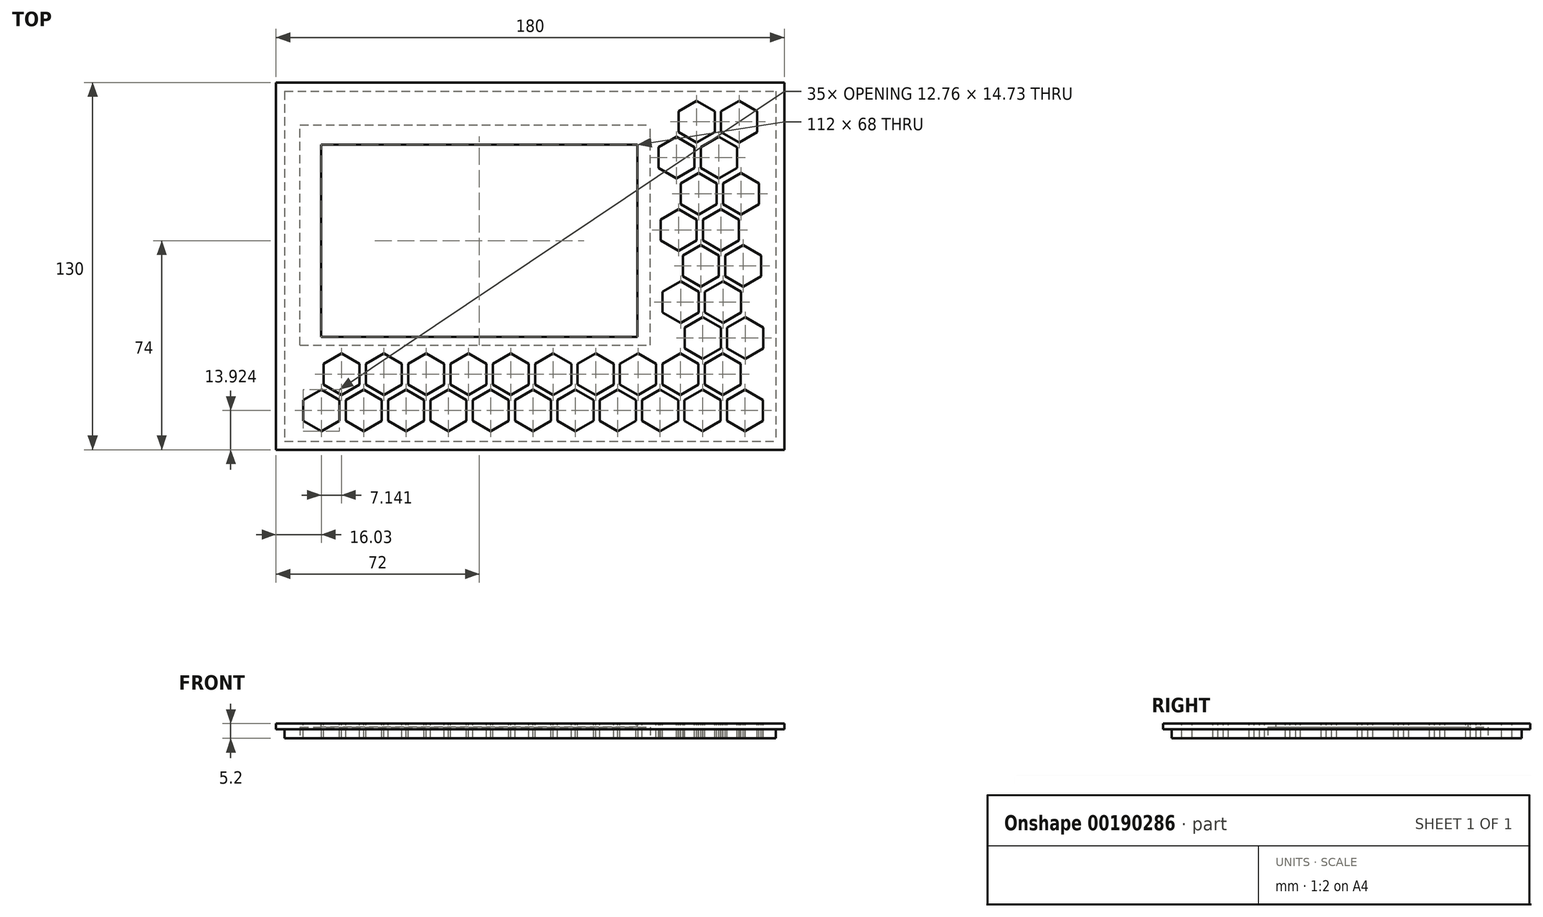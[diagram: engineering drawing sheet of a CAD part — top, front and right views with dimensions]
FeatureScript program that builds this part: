
annotation { "Feature Type Name" : "Feature", "Feature Type Description" : "" }
export const myFeature = defineFeature(function(context is Context, id is Id, definition is map)
    precondition{}
    {
        {
            var Q0;
            Q0=qCreatedBy(makeId("Top.planeOp"),FACE);
            var sketch = newSketch(context, id + "F0", { "sketchPlane" : qUnion([Q0])});
            skLineSegment(sketch, "E0.bottom", {"start": v(42.5, 28) * mm, "end": v(-42.5, 28) * mm});
            skLineSegment(sketch, "E0.top", {"start": v(42.5, -28) * mm, "end": v(-42.5, -28) * mm});
            skLineSegment(sketch, "E0.left", {"start": v(42.5, 28) * mm, "end": v(42.5, -28) * mm});
            skLineSegment(sketch, "E0.right", {"start": v(-42.5, 28) * mm, "end": v(-42.5, -28) * mm});
            skPoint(sketch, "E0.middle", {"position": v(0, 0) * mm});
            skCircle(sketch, "E1", {"center": v(-39, 24.5) * mm, "radius": 1.4 * mm});
            skCircle(sketch, "E2.MirrorC", {"center": v(-34.56, -24.5) * mm, "radius": 1.4 * mm});
            skCircle(sketch, "E3", {"center": v(19, 24.5) * mm, "radius": 1.4 * mm});
            skCircle(sketch, "E4.MirrorC", {"center": v(19, -24.7) * mm, "radius": 1.4 * mm});
            skSolve(sketch);
        }
        {
            var Q0;
            Q0=qCreatedBy(makeId("Top.planeOp"),FACE);
            var sketch = newSketch(context, id + "F1", { "sketchPlane" : qUnion([Q0])});
            skLineSegment(sketch, "E5.bottom", {"start": v(-90, 65) * mm, "end": v(90, 65) * mm});
            skLineSegment(sketch, "E5.top", {"start": v(-90, -65) * mm, "end": v(90, -65) * mm});
            skLineSegment(sketch, "E5.left", {"start": v(-90, 65) * mm, "end": v(-90, -65) * mm});
            skLineSegment(sketch, "E5.right", {"start": v(90, 65) * mm, "end": v(90, -65) * mm});
            skPoint(sketch, "E5.middle", {"position": v(0, 0) * mm});
            skLineSegment(sketch, "E6.bottom", {"start": v(-86.95, 61.95) * mm, "end": v(86.95, 61.95) * mm});
            skLineSegment(sketch, "E6.top", {"start": v(-86.95, -61.95) * mm, "end": v(86.95, -61.95) * mm});
            skLineSegment(sketch, "E6.left", {"start": v(-86.95, 61.95) * mm, "end": v(-86.95, -61.95) * mm});
            skLineSegment(sketch, "E6.right", {"start": v(86.95, 61.95) * mm, "end": v(86.95, -61.95) * mm});
            skSolve(sketch);
        }
        {
            var Q0;
            Q0=qCreatedBy(makeId("Top.planeOp"),FACE);
            var sketch = newSketch(context, id + "F2", { "sketchPlane" : qUnion([Q0])});
            skLineSegment(sketch, "E7.bottom", {"start": v(42.5, 50) * mm, "end": v(-81.5, 50) * mm});
            skLineSegment(sketch, "E7.top", {"start": v(42.5, -28) * mm, "end": v(-81.5, -28) * mm});
            skLineSegment(sketch, "E7.left", {"start": v(42.5, 50) * mm, "end": v(42.5, -28) * mm});
            skLineSegment(sketch, "E7.right", {"start": v(-81.5, 50) * mm, "end": v(-81.5, -28) * mm});
            skPoint(sketch, "E7.middle", {"position": v(0, 0) * mm});
            skSolve(sketch);
        }
        {
            var Q0;
            Q0=makeQuery(id+"F1.imprint","IMPRINT",FACE,{"disambiguationData":[TD([[makeQuery(id+"F1.imprint","IMPRINT",EDGE,{"derivedFrom":sQuery(id+"F1.wireOp",EDGE,"E5.bottom")}),-1.0]])]});
            var Q1;
            Q1=makeQuery(id+"F1.imprint","IMPRINT",FACE,{"disambiguationData":[TD([[makeQuery(id+"F1.imprint","IMPRINT",EDGE,{"derivedFrom":sQuery(id+"F1.wireOp",EDGE,"E6.bottom")}),-1.0]])]});
            extrude(context, id + "F3", {"entities" : qUnion([Q0, Q1]), "depth" : 2 * mm});
        }
        {
            var Q0;
            Q0=makeQuery(id+"F1.imprint","IMPRINT",FACE,{"disambiguationData":[TD([[makeQuery(id+"F1.imprint","IMPRINT",EDGE,{"derivedFrom":sQuery(id+"F1.wireOp",EDGE,"E6.bottom")}),-1.0]])]});
            extrude(context, id + "F4", {"entities" : qUnion([Q0]), "operationType" : NewBodyOperationType.ADD, "oppositeDirection" : true, "depth" : 3.2 * mm});
        }
        {
            var Q0;
            Q0=makeQuery(id+"F2.imprint","IMPRINT",FACE,{"disambiguationData":[TD([[makeQuery(id+"F2.imprint","IMPRINT",EDGE,{"derivedFrom":sQuery(id+"F2.wireOp",EDGE,"E7.bottom")}),1.0]])]});
            extrude(context, id + "F5", {"entities" : qUnion([Q0]), "operationType" : NewBodyOperationType.REMOVE, "endBound" : BoundingType.SYMMETRIC, "depth" : 25 * mm});
        }
        {
            var Q0;
            Q0=makeQuery(id+"F3.opExtrude","CAP_FACE",FACE,{"disambiguationData":[OSD([sQuery(id+"F1.wireOp",EDGE,"E5.bottom"),sQuery(id+"F1.wireOp",EDGE,"E5.top"),sQuery(id+"F1.wireOp",EDGE,"E5.left"),sQuery(id+"F1.wireOp",EDGE,"E5.right")])],"isStart":false});
            var sketch = newSketch(context, id + "F6", { "sketchPlane" : qUnion([Q0])});
            skPoint(sketch, "E8.0.5.0", {"position": v(78.65, 43.94) * mm});
            skCircle(sketch, "E8.0.6.1", {"center": v(73.98, 51.19) * mm, "radius": 6.38 * mm, "construction": true});
            skLineSegment(sketch, "E8.0.6.2", {"start": v(73.98, 43.82) * mm, "end": v(67.6, 47.5) * mm});
            skLineSegment(sketch, "E8.0.6.3", {"start": v(80.36, 47.5) * mm, "end": v(73.98, 43.82) * mm});
            skLineSegment(sketch, "E8.0.6.4", {"start": v(67.6, 54.87) * mm, "end": v(73.98, 58.56) * mm});
            skLineSegment(sketch, "E8.0.6.5", {"start": v(73.98, 58.56) * mm, "end": v(80.36, 54.87) * mm});
            skLineSegment(sketch, "E8.0.6.6", {"start": v(80.36, 54.87) * mm, "end": v(80.36, 47.5) * mm});
            skLineSegment(sketch, "E8.0.6.7", {"start": v(67.6, 47.5) * mm, "end": v(67.6, 54.87) * mm});
            skPoint(sketch, "E8.1.4.0", {"position": v(71.5, 31.16) * mm});
            skCircle(sketch, "E8.1.4.1", {"center": v(74.7, 25.64) * mm, "radius": 6.38 * mm, "construction": true});
            skLineSegment(sketch, "E8.1.4.2", {"start": v(74.7, 18.27) * mm, "end": v(68.32, 21.95) * mm});
            skLineSegment(sketch, "E8.1.4.3", {"start": v(81.08, 21.95) * mm, "end": v(74.7, 18.27) * mm});
            skLineSegment(sketch, "E8.1.4.4", {"start": v(68.32, 29.32) * mm, "end": v(74.7, 33) * mm});
            skLineSegment(sketch, "E8.1.4.5", {"start": v(74.7, 33) * mm, "end": v(81.08, 29.32) * mm});
            skLineSegment(sketch, "E8.1.4.6", {"start": v(81.08, 29.32) * mm, "end": v(81.08, 21.95) * mm});
            skLineSegment(sketch, "E8.1.4.7", {"start": v(68.32, 21.95) * mm, "end": v(68.32, 29.32) * mm});
            skPoint(sketch, "E8.1.5.0", {"position": v(63.65, 43.94) * mm});
            skCircle(sketch, "E8.1.5.1", {"center": v(66.84, 38.41) * mm, "radius": 6.38 * mm, "construction": true});
            skLineSegment(sketch, "E8.1.5.2", {"start": v(66.84, 31.05) * mm, "end": v(60.46, 34.73) * mm});
            skLineSegment(sketch, "E8.1.5.3", {"start": v(73.22, 34.73) * mm, "end": v(66.84, 31.05) * mm});
            skLineSegment(sketch, "E8.1.5.4", {"start": v(60.46, 42.1) * mm, "end": v(66.84, 45.78) * mm});
            skLineSegment(sketch, "E8.1.5.5", {"start": v(66.84, 45.78) * mm, "end": v(73.22, 42.1) * mm});
            skLineSegment(sketch, "E8.1.5.6", {"start": v(73.22, 42.1) * mm, "end": v(73.22, 34.73) * mm});
            skLineSegment(sketch, "E8.1.5.7", {"start": v(60.46, 34.73) * mm, "end": v(60.46, 42.1) * mm});
            skCircle(sketch, "E8.1.6.1", {"center": v(58.98, 51.19) * mm, "radius": 6.38 * mm, "construction": true});
            skLineSegment(sketch, "E8.1.6.2", {"start": v(58.98, 43.82) * mm, "end": v(52.6, 47.5) * mm});
            skLineSegment(sketch, "E8.1.6.3", {"start": v(65.36, 47.5) * mm, "end": v(58.98, 43.82) * mm});
            skLineSegment(sketch, "E8.1.6.4", {"start": v(52.6, 54.87) * mm, "end": v(58.98, 58.56) * mm});
            skLineSegment(sketch, "E8.1.6.5", {"start": v(58.98, 58.56) * mm, "end": v(65.36, 54.87) * mm});
            skLineSegment(sketch, "E8.1.6.6", {"start": v(65.36, 54.87) * mm, "end": v(65.36, 47.5) * mm});
            skLineSegment(sketch, "E8.1.6.7", {"start": v(52.6, 47.5) * mm, "end": v(52.6, 54.87) * mm});
            skPoint(sketch, "E8.2.2.0", {"position": v(72.23, 5.6) * mm});
            skCircle(sketch, "E8.2.2.1", {"center": v(75.42, 0.08) * mm, "radius": 6.38 * mm, "construction": true});
            skLineSegment(sketch, "E8.2.2.2", {"start": v(75.42, -7.28) * mm, "end": v(69.04, -3.6) * mm});
            skLineSegment(sketch, "E8.2.2.3", {"start": v(81.8, -3.6) * mm, "end": v(75.42, -7.28) * mm});
            skLineSegment(sketch, "E8.2.2.4", {"start": v(69.04, 3.77) * mm, "end": v(75.42, 7.45) * mm});
            skLineSegment(sketch, "E8.2.2.5", {"start": v(75.42, 7.45) * mm, "end": v(81.8, 3.77) * mm});
            skLineSegment(sketch, "E8.2.2.6", {"start": v(81.8, 3.77) * mm, "end": v(81.8, -3.6) * mm});
            skLineSegment(sketch, "E8.2.2.7", {"start": v(69.04, -3.6) * mm, "end": v(69.04, 3.77) * mm});
            skPoint(sketch, "E8.2.3.0", {"position": v(64.37, 18.39) * mm});
            skCircle(sketch, "E8.2.3.1", {"center": v(67.56, 12.86) * mm, "radius": 6.38 * mm, "construction": true});
            skLineSegment(sketch, "E8.2.3.2", {"start": v(67.56, 5.5) * mm, "end": v(61.18, 9.18) * mm});
            skLineSegment(sketch, "E8.2.3.3", {"start": v(73.94, 9.18) * mm, "end": v(67.56, 5.5) * mm});
            skLineSegment(sketch, "E8.2.3.4", {"start": v(61.18, 16.54) * mm, "end": v(67.56, 20.23) * mm});
            skLineSegment(sketch, "E8.2.3.5", {"start": v(67.56, 20.23) * mm, "end": v(73.94, 16.54) * mm});
            skLineSegment(sketch, "E8.2.3.6", {"start": v(73.94, 16.54) * mm, "end": v(73.94, 9.18) * mm});
            skLineSegment(sketch, "E8.2.3.7", {"start": v(61.18, 9.18) * mm, "end": v(61.18, 16.54) * mm});
            skPoint(sketch, "E8.2.4.0", {"position": v(56.5, 31.16) * mm});
            skCircle(sketch, "E8.2.4.1", {"center": v(59.7, 25.64) * mm, "radius": 6.38 * mm, "construction": true});
            skLineSegment(sketch, "E8.2.4.2", {"start": v(59.7, 18.27) * mm, "end": v(53.32, 21.95) * mm});
            skLineSegment(sketch, "E8.2.4.3", {"start": v(66.08, 21.95) * mm, "end": v(59.7, 18.27) * mm});
            skLineSegment(sketch, "E8.2.4.4", {"start": v(53.32, 29.32) * mm, "end": v(59.7, 33) * mm});
            skLineSegment(sketch, "E8.2.4.5", {"start": v(59.7, 33) * mm, "end": v(66.08, 29.32) * mm});
            skLineSegment(sketch, "E8.2.4.6", {"start": v(66.08, 29.32) * mm, "end": v(66.08, 21.95) * mm});
            skLineSegment(sketch, "E8.2.4.7", {"start": v(53.32, 21.95) * mm, "end": v(53.32, 29.32) * mm});
            skPoint(sketch, "E8.2.5.0", {"position": v(48.65, 43.94) * mm});
            skCircle(sketch, "E8.2.5.1", {"center": v(51.84, 38.41) * mm, "radius": 6.38 * mm, "construction": true});
            skLineSegment(sketch, "E8.2.5.2", {"start": v(51.84, 31.05) * mm, "end": v(45.46, 34.73) * mm});
            skLineSegment(sketch, "E8.2.5.3", {"start": v(58.22, 34.73) * mm, "end": v(51.84, 31.05) * mm});
            skLineSegment(sketch, "E8.2.5.4", {"start": v(45.46, 42.1) * mm, "end": v(51.84, 45.78) * mm});
            skLineSegment(sketch, "E8.2.5.5", {"start": v(51.84, 45.78) * mm, "end": v(58.22, 42.1) * mm});
            skLineSegment(sketch, "E8.2.5.6", {"start": v(58.22, 42.1) * mm, "end": v(58.22, 34.73) * mm});
            skLineSegment(sketch, "E8.2.5.7", {"start": v(45.46, 34.73) * mm, "end": v(45.46, 42.1) * mm});
            skPoint(sketch, "E8.3.0.0", {"position": v(72.95, -19.94) * mm});
            skCircle(sketch, "E8.3.0.1", {"center": v(76.13, -25.47) * mm, "radius": 6.38 * mm, "construction": true});
            skLineSegment(sketch, "E8.3.0.2", {"start": v(76.13, -32.83) * mm, "end": v(69.76, -29.15) * mm});
            skLineSegment(sketch, "E8.3.0.3", {"start": v(82.51, -29.15) * mm, "end": v(76.13, -32.83) * mm});
            skLineSegment(sketch, "E8.3.0.4", {"start": v(69.76, -21.78) * mm, "end": v(76.13, -18.1) * mm});
            skLineSegment(sketch, "E8.3.0.5", {"start": v(76.13, -18.1) * mm, "end": v(82.51, -21.78) * mm});
            skLineSegment(sketch, "E8.3.0.6", {"start": v(82.51, -21.78) * mm, "end": v(82.51, -29.15) * mm});
            skLineSegment(sketch, "E8.3.0.7", {"start": v(69.76, -29.15) * mm, "end": v(69.76, -21.78) * mm});
            skPoint(sketch, "E8.3.1.0", {"position": v(65.09, -7.17) * mm});
            skCircle(sketch, "E8.3.1.1", {"center": v(68.28, -12.7) * mm, "radius": 6.38 * mm, "construction": true});
            skLineSegment(sketch, "E8.3.1.2", {"start": v(68.28, -20.06) * mm, "end": v(61.9, -16.37) * mm});
            skLineSegment(sketch, "E8.3.1.3", {"start": v(74.65, -16.37) * mm, "end": v(68.28, -20.06) * mm});
            skLineSegment(sketch, "E8.3.1.4", {"start": v(61.9, -9) * mm, "end": v(68.28, -5.33) * mm});
            skLineSegment(sketch, "E8.3.1.5", {"start": v(68.28, -5.33) * mm, "end": v(74.65, -9) * mm});
            skLineSegment(sketch, "E8.3.1.6", {"start": v(74.65, -9) * mm, "end": v(74.65, -16.37) * mm});
            skLineSegment(sketch, "E8.3.1.7", {"start": v(61.9, -16.37) * mm, "end": v(61.9, -9) * mm});
            skPoint(sketch, "E8.3.2.0", {"position": v(57.23, 5.6) * mm});
            skCircle(sketch, "E8.3.2.1", {"center": v(60.42, 0.08) * mm, "radius": 6.38 * mm, "construction": true});
            skLineSegment(sketch, "E8.3.2.2", {"start": v(60.42, -7.28) * mm, "end": v(54.04, -3.6) * mm});
            skLineSegment(sketch, "E8.3.2.3", {"start": v(66.8, -3.6) * mm, "end": v(60.42, -7.28) * mm});
            skLineSegment(sketch, "E8.3.2.4", {"start": v(54.04, 3.77) * mm, "end": v(60.42, 7.45) * mm});
            skLineSegment(sketch, "E8.3.2.5", {"start": v(60.42, 7.45) * mm, "end": v(66.8, 3.77) * mm});
            skLineSegment(sketch, "E8.3.2.6", {"start": v(66.8, 3.77) * mm, "end": v(66.8, -3.6) * mm});
            skLineSegment(sketch, "E8.3.2.7", {"start": v(54.04, -3.6) * mm, "end": v(54.04, 3.77) * mm});
            skPoint(sketch, "E8.3.3.0", {"position": v(49.37, 18.39) * mm});
            skCircle(sketch, "E8.3.3.1", {"center": v(52.56, 12.86) * mm, "radius": 6.38 * mm, "construction": true});
            skLineSegment(sketch, "E8.3.3.2", {"start": v(52.56, 5.5) * mm, "end": v(46.18, 9.18) * mm});
            skLineSegment(sketch, "E8.3.3.3", {"start": v(58.94, 9.18) * mm, "end": v(52.56, 5.5) * mm});
            skLineSegment(sketch, "E8.3.3.4", {"start": v(46.18, 16.54) * mm, "end": v(52.56, 20.23) * mm});
            skLineSegment(sketch, "E8.3.3.5", {"start": v(52.56, 20.23) * mm, "end": v(58.94, 16.54) * mm});
            skLineSegment(sketch, "E8.3.3.6", {"start": v(58.94, 16.54) * mm, "end": v(58.94, 9.18) * mm});
            skLineSegment(sketch, "E8.3.3.7", {"start": v(46.18, 9.18) * mm, "end": v(46.18, 16.54) * mm});
            skPoint(sketch, "E8.4.0.0", {"position": v(57.95, -19.94) * mm});
            skCircle(sketch, "E8.4.0.1", {"center": v(61.13, -25.47) * mm, "radius": 6.38 * mm, "construction": true});
            skLineSegment(sketch, "E8.4.0.2", {"start": v(61.13, -32.83) * mm, "end": v(54.76, -29.15) * mm});
            skLineSegment(sketch, "E8.4.0.3", {"start": v(67.51, -29.15) * mm, "end": v(61.13, -32.83) * mm});
            skLineSegment(sketch, "E8.4.0.4", {"start": v(54.76, -21.78) * mm, "end": v(61.13, -18.1) * mm});
            skLineSegment(sketch, "E8.4.0.5", {"start": v(61.13, -18.1) * mm, "end": v(67.51, -21.78) * mm});
            skLineSegment(sketch, "E8.4.0.6", {"start": v(67.51, -21.78) * mm, "end": v(67.51, -29.15) * mm});
            skLineSegment(sketch, "E8.4.0.7", {"start": v(54.76, -29.15) * mm, "end": v(54.76, -21.78) * mm});
            skPoint(sketch, "E8.4.1.0", {"position": v(50.09, -7.17) * mm});
            skCircle(sketch, "E8.4.1.1", {"center": v(53.28, -12.7) * mm, "radius": 6.38 * mm, "construction": true});
            skLineSegment(sketch, "E8.4.1.2", {"start": v(53.28, -20.06) * mm, "end": v(46.9, -16.37) * mm});
            skLineSegment(sketch, "E8.4.1.3", {"start": v(59.65, -16.37) * mm, "end": v(53.28, -20.06) * mm});
            skLineSegment(sketch, "E8.4.1.4", {"start": v(46.9, -9) * mm, "end": v(53.28, -5.33) * mm});
            skLineSegment(sketch, "E8.4.1.5", {"start": v(53.28, -5.33) * mm, "end": v(59.65, -9) * mm});
            skLineSegment(sketch, "E8.4.1.6", {"start": v(59.65, -9) * mm, "end": v(59.65, -16.37) * mm});
            skLineSegment(sketch, "E8.4.1.7", {"start": v(46.9, -16.37) * mm, "end": v(46.9, -9) * mm});
            skPoint(sketch, "E9.3.0.0", {"position": v(72.84, -45.55) * mm});
            skCircle(sketch, "E9.3.0.1", {"center": v(76.03, -51.08) * mm, "radius": 6.38 * mm, "construction": true});
            skLineSegment(sketch, "E9.3.0.2", {"start": v(76.03, -58.44) * mm, "end": v(69.65, -54.76) * mm});
            skLineSegment(sketch, "E9.3.0.3", {"start": v(82.4, -54.76) * mm, "end": v(76.03, -58.44) * mm});
            skLineSegment(sketch, "E9.3.0.4", {"start": v(69.65, -47.4) * mm, "end": v(76.03, -43.71) * mm});
            skLineSegment(sketch, "E9.3.0.5", {"start": v(76.03, -43.71) * mm, "end": v(82.4, -47.4) * mm});
            skLineSegment(sketch, "E9.3.0.6", {"start": v(82.4, -47.4) * mm, "end": v(82.4, -54.76) * mm});
            skLineSegment(sketch, "E9.3.0.7", {"start": v(69.65, -54.76) * mm, "end": v(69.65, -47.4) * mm});
            skPoint(sketch, "E9.3.1.0", {"position": v(64.98, -32.78) * mm});
            skCircle(sketch, "E9.3.1.1", {"center": v(68.17, -38.3) * mm, "radius": 6.38 * mm, "construction": true});
            skLineSegment(sketch, "E9.3.1.2", {"start": v(68.17, -45.67) * mm, "end": v(61.8, -41.98) * mm});
            skLineSegment(sketch, "E9.3.1.3", {"start": v(74.55, -41.98) * mm, "end": v(68.17, -45.67) * mm});
            skLineSegment(sketch, "E9.3.1.4", {"start": v(61.8, -34.62) * mm, "end": v(68.17, -30.93) * mm});
            skLineSegment(sketch, "E9.3.1.5", {"start": v(68.17, -30.93) * mm, "end": v(74.55, -34.62) * mm});
            skLineSegment(sketch, "E9.3.1.6", {"start": v(74.55, -34.62) * mm, "end": v(74.55, -41.98) * mm});
            skLineSegment(sketch, "E9.3.1.7", {"start": v(61.8, -41.98) * mm, "end": v(61.8, -34.62) * mm});
            skPoint(sketch, "E9.4.0.0", {"position": v(57.84, -45.55) * mm});
            skCircle(sketch, "E9.4.0.1", {"center": v(61.03, -51.08) * mm, "radius": 6.38 * mm, "construction": true});
            skLineSegment(sketch, "E9.4.0.2", {"start": v(61.03, -58.44) * mm, "end": v(54.65, -54.76) * mm});
            skLineSegment(sketch, "E9.4.0.3", {"start": v(67.4, -54.76) * mm, "end": v(61.03, -58.44) * mm});
            skLineSegment(sketch, "E9.4.0.4", {"start": v(54.65, -47.4) * mm, "end": v(61.03, -43.71) * mm});
            skLineSegment(sketch, "E9.4.0.5", {"start": v(61.03, -43.71) * mm, "end": v(67.4, -47.4) * mm});
            skLineSegment(sketch, "E9.4.0.6", {"start": v(67.4, -47.4) * mm, "end": v(67.4, -54.76) * mm});
            skLineSegment(sketch, "E9.4.0.7", {"start": v(54.65, -54.76) * mm, "end": v(54.65, -47.4) * mm});
            skPoint(sketch, "E9.4.1.0", {"position": v(49.98, -32.78) * mm});
            skCircle(sketch, "E9.4.1.1", {"center": v(53.17, -38.3) * mm, "radius": 6.38 * mm, "construction": true});
            skLineSegment(sketch, "E9.4.1.2", {"start": v(53.17, -45.67) * mm, "end": v(46.8, -41.98) * mm});
            skLineSegment(sketch, "E9.4.1.3", {"start": v(59.55, -41.98) * mm, "end": v(53.17, -45.67) * mm});
            skLineSegment(sketch, "E9.4.1.4", {"start": v(46.8, -34.62) * mm, "end": v(53.17, -30.93) * mm});
            skLineSegment(sketch, "E9.4.1.5", {"start": v(53.17, -30.93) * mm, "end": v(59.55, -34.62) * mm});
            skLineSegment(sketch, "E9.4.1.6", {"start": v(59.55, -34.62) * mm, "end": v(59.55, -41.98) * mm});
            skLineSegment(sketch, "E9.4.1.7", {"start": v(46.8, -41.98) * mm, "end": v(46.8, -34.62) * mm});
            skPoint(sketch, "E9.5.0.0", {"position": v(42.84, -45.55) * mm});
            skCircle(sketch, "E9.5.0.1", {"center": v(46.03, -51.08) * mm, "radius": 6.38 * mm, "construction": true});
            skLineSegment(sketch, "E9.5.0.2", {"start": v(46.03, -58.44) * mm, "end": v(39.65, -54.76) * mm});
            skLineSegment(sketch, "E9.5.0.3", {"start": v(52.4, -54.76) * mm, "end": v(46.03, -58.44) * mm});
            skLineSegment(sketch, "E9.5.0.4", {"start": v(39.65, -47.4) * mm, "end": v(46.03, -43.71) * mm});
            skLineSegment(sketch, "E9.5.0.5", {"start": v(46.03, -43.71) * mm, "end": v(52.4, -47.4) * mm});
            skLineSegment(sketch, "E9.5.0.6", {"start": v(52.4, -47.4) * mm, "end": v(52.4, -54.76) * mm});
            skLineSegment(sketch, "E9.5.0.7", {"start": v(39.65, -54.76) * mm, "end": v(39.65, -47.4) * mm});
            skPoint(sketch, "E9.5.1.0", {"position": v(34.98, -32.78) * mm});
            skCircle(sketch, "E9.5.1.1", {"center": v(38.17, -38.3) * mm, "radius": 6.38 * mm, "construction": true});
            skLineSegment(sketch, "E9.5.1.2", {"start": v(38.17, -45.67) * mm, "end": v(31.8, -41.98) * mm});
            skLineSegment(sketch, "E9.5.1.3", {"start": v(44.55, -41.98) * mm, "end": v(38.17, -45.67) * mm});
            skLineSegment(sketch, "E9.5.1.4", {"start": v(31.8, -34.62) * mm, "end": v(38.17, -30.93) * mm});
            skLineSegment(sketch, "E9.5.1.5", {"start": v(38.17, -30.93) * mm, "end": v(44.55, -34.62) * mm});
            skLineSegment(sketch, "E9.5.1.6", {"start": v(44.55, -34.62) * mm, "end": v(44.55, -41.98) * mm});
            skLineSegment(sketch, "E9.5.1.7", {"start": v(31.8, -41.98) * mm, "end": v(31.8, -34.62) * mm});
            skPoint(sketch, "E9.6.0.0", {"position": v(27.84, -45.55) * mm});
            skCircle(sketch, "E9.6.0.1", {"center": v(31.03, -51.08) * mm, "radius": 6.38 * mm, "construction": true});
            skLineSegment(sketch, "E9.6.0.2", {"start": v(31.03, -58.44) * mm, "end": v(24.65, -54.76) * mm});
            skLineSegment(sketch, "E9.6.0.3", {"start": v(37.4, -54.76) * mm, "end": v(31.03, -58.44) * mm});
            skLineSegment(sketch, "E9.6.0.4", {"start": v(24.65, -47.4) * mm, "end": v(31.03, -43.71) * mm});
            skLineSegment(sketch, "E9.6.0.5", {"start": v(31.03, -43.71) * mm, "end": v(37.4, -47.4) * mm});
            skLineSegment(sketch, "E9.6.0.6", {"start": v(37.4, -47.4) * mm, "end": v(37.4, -54.76) * mm});
            skLineSegment(sketch, "E9.6.0.7", {"start": v(24.65, -54.76) * mm, "end": v(24.65, -47.4) * mm});
            skPoint(sketch, "E9.6.1.0", {"position": v(19.98, -32.78) * mm});
            skCircle(sketch, "E9.6.1.1", {"center": v(23.17, -38.3) * mm, "radius": 6.38 * mm, "construction": true});
            skLineSegment(sketch, "E9.6.1.2", {"start": v(23.17, -45.67) * mm, "end": v(16.8, -41.98) * mm});
            skLineSegment(sketch, "E9.6.1.3", {"start": v(29.55, -41.98) * mm, "end": v(23.17, -45.67) * mm});
            skLineSegment(sketch, "E9.6.1.4", {"start": v(16.8, -34.62) * mm, "end": v(23.17, -30.93) * mm});
            skLineSegment(sketch, "E9.6.1.5", {"start": v(23.17, -30.93) * mm, "end": v(29.55, -34.62) * mm});
            skLineSegment(sketch, "E9.6.1.6", {"start": v(29.55, -34.62) * mm, "end": v(29.55, -41.98) * mm});
            skLineSegment(sketch, "E9.6.1.7", {"start": v(16.8, -41.98) * mm, "end": v(16.8, -34.62) * mm});
            skPoint(sketch, "E9.7.0.0", {"position": v(12.84, -45.55) * mm});
            skCircle(sketch, "E9.7.0.1", {"center": v(16.03, -51.08) * mm, "radius": 6.38 * mm, "construction": true});
            skLineSegment(sketch, "E9.7.0.2", {"start": v(16.03, -58.44) * mm, "end": v(9.65, -54.76) * mm});
            skLineSegment(sketch, "E9.7.0.3", {"start": v(22.4, -54.76) * mm, "end": v(16.03, -58.44) * mm});
            skLineSegment(sketch, "E9.7.0.4", {"start": v(9.65, -47.4) * mm, "end": v(16.03, -43.71) * mm});
            skLineSegment(sketch, "E9.7.0.5", {"start": v(16.03, -43.71) * mm, "end": v(22.4, -47.4) * mm});
            skLineSegment(sketch, "E9.7.0.6", {"start": v(22.4, -47.4) * mm, "end": v(22.4, -54.76) * mm});
            skLineSegment(sketch, "E9.7.0.7", {"start": v(9.65, -54.76) * mm, "end": v(9.65, -47.4) * mm});
            skPoint(sketch, "E9.7.1.0", {"position": v(4.98, -32.78) * mm});
            skCircle(sketch, "E9.7.1.1", {"center": v(8.17, -38.3) * mm, "radius": 6.38 * mm, "construction": true});
            skLineSegment(sketch, "E9.7.1.2", {"start": v(8.17, -45.67) * mm, "end": v(1.8, -41.98) * mm});
            skLineSegment(sketch, "E9.7.1.3", {"start": v(14.55, -41.98) * mm, "end": v(8.17, -45.67) * mm});
            skLineSegment(sketch, "E9.7.1.4", {"start": v(1.8, -34.62) * mm, "end": v(8.17, -30.93) * mm});
            skLineSegment(sketch, "E9.7.1.5", {"start": v(8.17, -30.93) * mm, "end": v(14.55, -34.62) * mm});
            skLineSegment(sketch, "E9.7.1.6", {"start": v(14.55, -34.62) * mm, "end": v(14.55, -41.98) * mm});
            skLineSegment(sketch, "E9.7.1.7", {"start": v(1.8, -41.98) * mm, "end": v(1.8, -34.62) * mm});
            skPoint(sketch, "E9.8.0.0", {"position": v(-2.16, -45.55) * mm});
            skCircle(sketch, "E9.8.0.1", {"center": v(1.03, -51.08) * mm, "radius": 6.38 * mm, "construction": true});
            skLineSegment(sketch, "E9.8.0.2", {"start": v(1.03, -58.44) * mm, "end": v(-5.35, -54.76) * mm});
            skLineSegment(sketch, "E9.8.0.3", {"start": v(7.4, -54.76) * mm, "end": v(1.03, -58.44) * mm});
            skLineSegment(sketch, "E9.8.0.4", {"start": v(-5.35, -47.4) * mm, "end": v(1.03, -43.71) * mm});
            skLineSegment(sketch, "E9.8.0.5", {"start": v(1.03, -43.71) * mm, "end": v(7.4, -47.4) * mm});
            skLineSegment(sketch, "E9.8.0.6", {"start": v(7.4, -47.4) * mm, "end": v(7.4, -54.76) * mm});
            skLineSegment(sketch, "E9.8.0.7", {"start": v(-5.35, -54.76) * mm, "end": v(-5.35, -47.4) * mm});
            skPoint(sketch, "E9.8.1.0", {"position": v(-10.02, -32.78) * mm});
            skCircle(sketch, "E9.8.1.1", {"center": v(-6.83, -38.3) * mm, "radius": 6.38 * mm, "construction": true});
            skLineSegment(sketch, "E9.8.1.2", {"start": v(-6.83, -45.67) * mm, "end": v(-13.2, -41.98) * mm});
            skLineSegment(sketch, "E9.8.1.3", {"start": v(-0.45, -41.98) * mm, "end": v(-6.83, -45.67) * mm});
            skLineSegment(sketch, "E9.8.1.4", {"start": v(-13.2, -34.62) * mm, "end": v(-6.83, -30.93) * mm});
            skLineSegment(sketch, "E9.8.1.5", {"start": v(-6.83, -30.93) * mm, "end": v(-0.45, -34.62) * mm});
            skLineSegment(sketch, "E9.8.1.6", {"start": v(-0.45, -34.62) * mm, "end": v(-0.45, -41.98) * mm});
            skLineSegment(sketch, "E9.8.1.7", {"start": v(-13.2, -41.98) * mm, "end": v(-13.2, -34.62) * mm});
            skPoint(sketch, "E9.9.0.0", {"position": v(-17.16, -45.55) * mm});
            skCircle(sketch, "E9.9.0.1", {"center": v(-13.97, -51.08) * mm, "radius": 6.38 * mm, "construction": true});
            skLineSegment(sketch, "E9.9.0.2", {"start": v(-13.97, -58.44) * mm, "end": v(-20.35, -54.76) * mm});
            skLineSegment(sketch, "E9.9.0.3", {"start": v(-7.6, -54.76) * mm, "end": v(-13.97, -58.44) * mm});
            skLineSegment(sketch, "E9.9.0.4", {"start": v(-20.35, -47.4) * mm, "end": v(-13.97, -43.71) * mm});
            skLineSegment(sketch, "E9.9.0.5", {"start": v(-13.97, -43.71) * mm, "end": v(-7.6, -47.4) * mm});
            skLineSegment(sketch, "E9.9.0.6", {"start": v(-7.6, -47.4) * mm, "end": v(-7.6, -54.76) * mm});
            skLineSegment(sketch, "E9.9.0.7", {"start": v(-20.35, -54.76) * mm, "end": v(-20.35, -47.4) * mm});
            skPoint(sketch, "E9.9.1.0", {"position": v(-25.02, -32.78) * mm});
            skCircle(sketch, "E9.9.1.1", {"center": v(-21.83, -38.3) * mm, "radius": 6.38 * mm, "construction": true});
            skLineSegment(sketch, "E9.9.1.2", {"start": v(-21.83, -45.67) * mm, "end": v(-28.2, -41.98) * mm});
            skLineSegment(sketch, "E9.9.1.3", {"start": v(-15.45, -41.98) * mm, "end": v(-21.83, -45.67) * mm});
            skLineSegment(sketch, "E9.9.1.4", {"start": v(-28.2, -34.62) * mm, "end": v(-21.83, -30.93) * mm});
            skLineSegment(sketch, "E9.9.1.5", {"start": v(-21.83, -30.93) * mm, "end": v(-15.45, -34.62) * mm});
            skLineSegment(sketch, "E9.9.1.6", {"start": v(-15.45, -34.62) * mm, "end": v(-15.45, -41.98) * mm});
            skLineSegment(sketch, "E9.9.1.7", {"start": v(-28.2, -41.98) * mm, "end": v(-28.2, -34.62) * mm});
            skPoint(sketch, "E9.10.0.0", {"position": v(-32.16, -45.55) * mm});
            skCircle(sketch, "E9.10.0.1", {"center": v(-28.97, -51.08) * mm, "radius": 6.38 * mm, "construction": true});
            skLineSegment(sketch, "E9.10.0.2", {"start": v(-28.97, -58.44) * mm, "end": v(-35.35, -54.76) * mm});
            skLineSegment(sketch, "E9.10.0.3", {"start": v(-22.6, -54.76) * mm, "end": v(-28.97, -58.44) * mm});
            skLineSegment(sketch, "E9.10.0.4", {"start": v(-35.35, -47.4) * mm, "end": v(-28.97, -43.71) * mm});
            skLineSegment(sketch, "E9.10.0.5", {"start": v(-28.97, -43.71) * mm, "end": v(-22.6, -47.4) * mm});
            skLineSegment(sketch, "E9.10.0.6", {"start": v(-22.6, -47.4) * mm, "end": v(-22.6, -54.76) * mm});
            skLineSegment(sketch, "E9.10.0.7", {"start": v(-35.35, -54.76) * mm, "end": v(-35.35, -47.4) * mm});
            skPoint(sketch, "E9.10.1.0", {"position": v(-40.02, -32.78) * mm});
            skCircle(sketch, "E9.10.1.1", {"center": v(-36.83, -38.3) * mm, "radius": 6.38 * mm, "construction": true});
            skLineSegment(sketch, "E9.10.1.2", {"start": v(-36.83, -45.67) * mm, "end": v(-43.2, -41.98) * mm});
            skLineSegment(sketch, "E9.10.1.3", {"start": v(-30.45, -41.98) * mm, "end": v(-36.83, -45.67) * mm});
            skLineSegment(sketch, "E9.10.1.4", {"start": v(-43.2, -34.62) * mm, "end": v(-36.83, -30.93) * mm});
            skLineSegment(sketch, "E9.10.1.5", {"start": v(-36.83, -30.93) * mm, "end": v(-30.45, -34.62) * mm});
            skLineSegment(sketch, "E9.10.1.6", {"start": v(-30.45, -34.62) * mm, "end": v(-30.45, -41.98) * mm});
            skLineSegment(sketch, "E9.10.1.7", {"start": v(-43.2, -41.98) * mm, "end": v(-43.2, -34.62) * mm});
            skPoint(sketch, "E9.11.0.0", {"position": v(-47.16, -45.55) * mm});
            skCircle(sketch, "E9.11.0.1", {"center": v(-43.97, -51.08) * mm, "radius": 6.38 * mm, "construction": true});
            skLineSegment(sketch, "E9.11.0.2", {"start": v(-43.97, -58.44) * mm, "end": v(-50.35, -54.76) * mm});
            skLineSegment(sketch, "E9.11.0.3", {"start": v(-37.6, -54.76) * mm, "end": v(-43.97, -58.44) * mm});
            skLineSegment(sketch, "E9.11.0.4", {"start": v(-50.35, -47.4) * mm, "end": v(-43.97, -43.71) * mm});
            skLineSegment(sketch, "E9.11.0.5", {"start": v(-43.97, -43.71) * mm, "end": v(-37.6, -47.4) * mm});
            skLineSegment(sketch, "E9.11.0.6", {"start": v(-37.6, -47.4) * mm, "end": v(-37.6, -54.76) * mm});
            skLineSegment(sketch, "E9.11.0.7", {"start": v(-50.35, -54.76) * mm, "end": v(-50.35, -47.4) * mm});
            skPoint(sketch, "E9.11.1.0", {"position": v(-55.02, -32.78) * mm});
            skCircle(sketch, "E9.11.1.1", {"center": v(-51.83, -38.3) * mm, "radius": 6.38 * mm, "construction": true});
            skLineSegment(sketch, "E9.11.1.2", {"start": v(-51.83, -45.67) * mm, "end": v(-58.2, -41.98) * mm});
            skLineSegment(sketch, "E9.11.1.3", {"start": v(-45.45, -41.98) * mm, "end": v(-51.83, -45.67) * mm});
            skLineSegment(sketch, "E9.11.1.4", {"start": v(-58.2, -34.62) * mm, "end": v(-51.83, -30.93) * mm});
            skLineSegment(sketch, "E9.11.1.5", {"start": v(-51.83, -30.93) * mm, "end": v(-45.45, -34.62) * mm});
            skLineSegment(sketch, "E9.11.1.6", {"start": v(-45.45, -34.62) * mm, "end": v(-45.45, -41.98) * mm});
            skLineSegment(sketch, "E9.11.1.7", {"start": v(-58.2, -41.98) * mm, "end": v(-58.2, -34.62) * mm});
            skPoint(sketch, "E9.12.0.0", {"position": v(-62.16, -45.55) * mm});
            skCircle(sketch, "E9.12.0.1", {"center": v(-58.97, -51.08) * mm, "radius": 6.38 * mm, "construction": true});
            skLineSegment(sketch, "E9.12.0.2", {"start": v(-58.97, -58.44) * mm, "end": v(-65.35, -54.76) * mm});
            skLineSegment(sketch, "E9.12.0.3", {"start": v(-52.6, -54.76) * mm, "end": v(-58.97, -58.44) * mm});
            skLineSegment(sketch, "E9.12.0.4", {"start": v(-65.35, -47.4) * mm, "end": v(-58.97, -43.71) * mm});
            skLineSegment(sketch, "E9.12.0.5", {"start": v(-58.97, -43.71) * mm, "end": v(-52.6, -47.4) * mm});
            skLineSegment(sketch, "E9.12.0.6", {"start": v(-52.6, -47.4) * mm, "end": v(-52.6, -54.76) * mm});
            skLineSegment(sketch, "E9.12.0.7", {"start": v(-65.35, -54.76) * mm, "end": v(-65.35, -47.4) * mm});
            skPoint(sketch, "E9.12.1.0", {"position": v(-70.02, -32.78) * mm});
            skCircle(sketch, "E9.12.1.1", {"center": v(-66.83, -38.3) * mm, "radius": 6.38 * mm, "construction": true});
            skLineSegment(sketch, "E9.12.1.2", {"start": v(-66.83, -45.67) * mm, "end": v(-73.2, -41.98) * mm});
            skLineSegment(sketch, "E9.12.1.3", {"start": v(-60.45, -41.98) * mm, "end": v(-66.83, -45.67) * mm});
            skLineSegment(sketch, "E9.12.1.4", {"start": v(-73.2, -34.62) * mm, "end": v(-66.83, -30.93) * mm});
            skLineSegment(sketch, "E9.12.1.5", {"start": v(-66.83, -30.93) * mm, "end": v(-60.45, -34.62) * mm});
            skLineSegment(sketch, "E9.12.1.6", {"start": v(-60.45, -34.62) * mm, "end": v(-60.45, -41.98) * mm});
            skLineSegment(sketch, "E9.12.1.7", {"start": v(-73.2, -41.98) * mm, "end": v(-73.2, -34.62) * mm});
            skPoint(sketch, "E9.13.0.0", {"position": v(-77.16, -45.55) * mm});
            skCircle(sketch, "E9.13.0.1", {"center": v(-73.97, -51.08) * mm, "radius": 6.38 * mm, "construction": true});
            skLineSegment(sketch, "E9.13.0.2", {"start": v(-73.97, -58.44) * mm, "end": v(-80.35, -54.76) * mm});
            skLineSegment(sketch, "E9.13.0.3", {"start": v(-67.6, -54.76) * mm, "end": v(-73.97, -58.44) * mm});
            skLineSegment(sketch, "E9.13.0.4", {"start": v(-80.35, -47.4) * mm, "end": v(-73.97, -43.71) * mm});
            skLineSegment(sketch, "E9.13.0.5", {"start": v(-73.97, -43.71) * mm, "end": v(-67.6, -47.4) * mm});
            skLineSegment(sketch, "E9.13.0.6", {"start": v(-67.6, -47.4) * mm, "end": v(-67.6, -54.76) * mm});
            skLineSegment(sketch, "E9.13.0.7", {"start": v(-80.35, -54.76) * mm, "end": v(-80.35, -47.4) * mm});
            skSolve(sketch);
        }
        {
            var Q0;
            Q0 = qSketchRegion(id + "F6", true);
            extrude(context, id + "F7", {"entities" : qUnion([Q0]), "operationType" : NewBodyOperationType.REMOVE, "endBound" : BoundingType.THROUGH_ALL, "oppositeDirection" : true, "depth" : 25 * mm});
        }
        {
            var Q0;
            Q0=makeQuery(id+"F3.opExtrude","CAP_FACE",FACE,{"disambiguationData":[OSD([sQuery(id+"F1.wireOp",EDGE,"E5.bottom"),sQuery(id+"F1.wireOp",EDGE,"E5.top"),sQuery(id+"F1.wireOp",EDGE,"E5.left"),sQuery(id+"F1.wireOp",EDGE,"E5.right")])],"isStart":false});
            var sketch = newSketch(context, id + "F8", { "sketchPlane" : qUnion([Q0])});
            skLineSegment(sketch, "E10.bottom", {"start": v(38, -25) * mm, "end": v(-74, -25) * mm});
            skLineSegment(sketch, "E10.top", {"start": v(38, 43) * mm, "end": v(-74, 43) * mm});
            skLineSegment(sketch, "E10.left", {"start": v(38, -25) * mm, "end": v(38, 43) * mm});
            skLineSegment(sketch, "E10.right", {"start": v(-74, -25) * mm, "end": v(-74, 43) * mm});
            skLineSegment(sketch, "E11.0", {"start": v(42.5, -28) * mm, "end": v(-81.5, -28) * mm});
            skLineSegment(sketch, "E12.0", {"start": v(42.5, 50) * mm, "end": v(42.5, -28) * mm});
            skLineSegment(sketch, "E13.0", {"start": v(-81.5, 50) * mm, "end": v(-81.5, -28) * mm});
            skLineSegment(sketch, "E14.0", {"start": v(42.5, 50) * mm, "end": v(-81.5, 50) * mm});
            skSolve(sketch);
        }
        {
            var Q0;
            Q0 = qSketchRegion(id + "F8", true);
            extrude(context, id + "F9", {"entities" : qUnion([Q0]), "operationType" : NewBodyOperationType.ADD, "oppositeDirection" : true, "depth" : 1.2 * mm});
        }
    });
